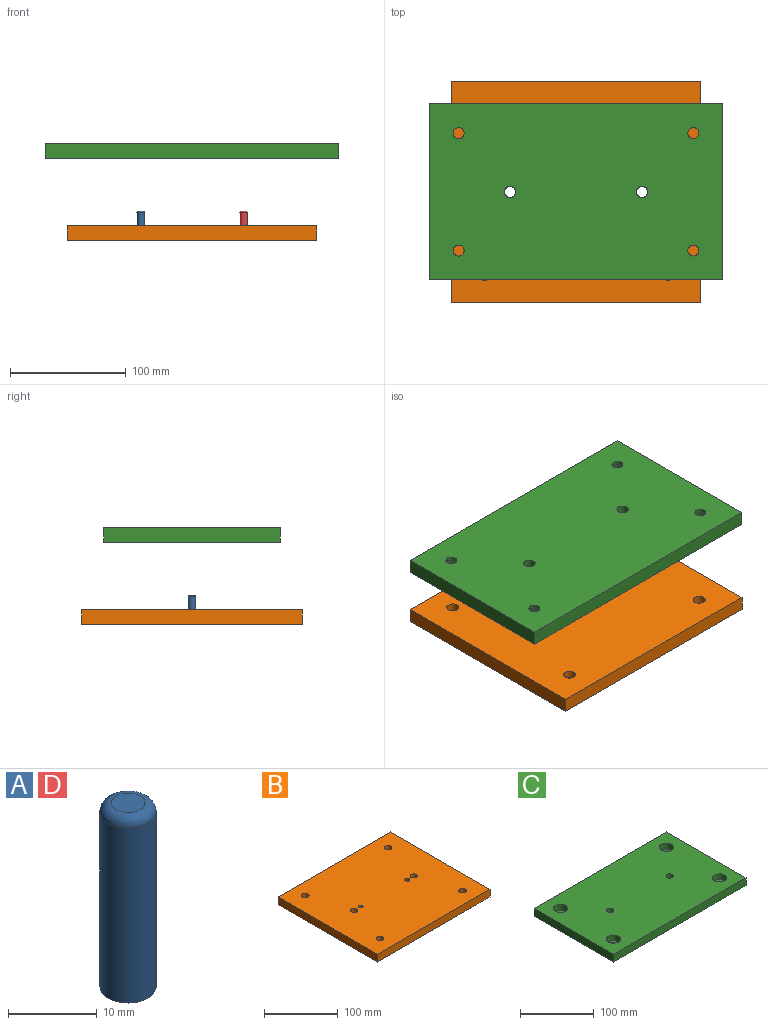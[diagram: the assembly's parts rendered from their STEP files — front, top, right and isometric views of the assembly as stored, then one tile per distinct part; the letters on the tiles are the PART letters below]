
ASSEMBLY  parts=4 mates=3
PART A: 4 faces, bbox 6.9x6.9x25.4 mm
  f0: cylinder r=3.17mm len=24.13mm, axis (0,0,-1), area 481.4mm2, adj f2,f3
  f1: plane 3.81x3.81mm, normal (0,0,1), area 11.4mm2, adj f3
  f2: plane 6.35x6.35mm, normal (0,0,-1), area 31.7mm2, adj f0
  f3: torus R=1.91mm, axis (0,0,1), area 34mm2, adj f0,f1
PART B: 22 faces, bbox 215.9x190.5x12.7 mm
  f0: plane 190.5x12.7mm, normal (-1,0,0), area 2419.3mm2, adj f1,f3,f4,f5
  f1: plane 215.9x12.7mm, normal (0,-1,0), area 2741.9mm2, adj f0,f2,f4,f5
  f2: plane 190.5x12.7mm, normal (1,0,0), area 2419.3mm2, adj f1,f3,f4,f5
  f3: plane 215.9x12.7mm, normal (0,1,0), area 2741.9mm2, adj f0,f2,f4,f5
  f4: plane 215.9x190.5mm, normal (0,0,1), area 40598.8mm2, adj f0,f1,f2,f3,f8,f11,f14,f17
  f5: plane 215.9x190.5mm, normal (0,0,-1), area 40791.3mm2, adj f0,f1,f2,f3,f6,f9,f12,f15
  f6: cylinder r=3.24mm len=6.48mm, axis (0,0,1), area 116.3mm2, adj f5,f7
  f7: plane 10.16x10.16mm, normal (0,0,1), area 48.1mm2, adj f6,f8
  f8: cylinder r=5.08mm len=10.16mm, axis (0,0,1), area 223mm2, adj f4,f7
  f9: cylinder r=3.24mm len=6.48mm, axis (0,0,1), area 116.3mm2, adj f5,f10
  f10: plane 10.16x10.16mm, normal (0,0,1), area 48.1mm2, adj f9,f11
  f11: cylinder r=5.08mm len=10.16mm, axis (0,0,1), area 223mm2, adj f4,f10
  f12: cylinder r=3.24mm len=6.48mm, axis (0,0,1), area 116.3mm2, adj f5,f13
  f13: plane 10.16x10.16mm, normal (0,0,1), area 48.1mm2, adj f12,f14
  f14: cylinder r=5.08mm len=10.16mm, axis (0,0,1), area 223mm2, adj f4,f13
  f15: cylinder r=3.24mm len=6.48mm, axis (0,0,1), area 116.3mm2, adj f5,f16
  f16: plane 10.16x10.16mm, normal (0,0,1), area 48.1mm2, adj f15,f17
  f17: cylinder r=5.08mm len=10.16mm, axis (0,0,1), area 223mm2, adj f4,f16
  f18: cylinder r=3.17mm len=12.7mm, axis (0,0,1), area 253.4mm2, adj f4,f5
  f19: cylinder r=3.17mm len=12.7mm, axis (0,0,1), area 253.4mm2, adj f4,f5
  f20: cylinder r=4.76mm len=12.7mm, axis (0,0,1), area 380mm2, adj f4,f5
  f21: cylinder r=4.76mm len=12.7mm, axis (0,0,1), area 380mm2, adj f4,f5
PART C: 20 faces, bbox 254x152.4x12.7 mm
  f0: plane 152.4x12.7mm, normal (-1,0,0), area 1935.5mm2, adj f1,f3,f4,f5
  f1: plane 254x12.7mm, normal (0,-1,0), area 3225.8mm2, adj f0,f2,f4,f5
  f2: plane 152.4x12.7mm, normal (1,0,0), area 1935.5mm2, adj f1,f3,f4,f5
  f3: plane 254x12.7mm, normal (0,1,0), area 3225.8mm2, adj f0,f2,f4,f5
  f4: plane 254x152.4mm, normal (0,0,1), area 37412.2mm2, adj f0,f1,f2,f3,f8,f11,f14,f17
  f5: plane 254x152.4mm, normal (0,0,-1), area 38267.3mm2, adj f0,f1,f2,f3,f6,f9,f12,f15
  f6: cylinder r=4.76mm len=9.53mm, axis (0,0,1), area 95mm2, adj f5,f7
  f7: plane 19.05x19.05mm, normal (0,0,1), area 213.8mm2, adj f6,f8
  f8: cylinder r=9.53mm len=19.05mm, axis (0,0,1), area 570mm2, adj f4,f7
  f9: cylinder r=4.76mm len=9.53mm, axis (0,0,1), area 95mm2, adj f5,f10
  f10: plane 19.05x19.05mm, normal (0,0,1), area 213.8mm2, adj f9,f11
  f11: cylinder r=9.53mm len=19.05mm, axis (0,0,1), area 570mm2, adj f4,f10
  f12: cylinder r=4.76mm len=9.53mm, axis (0,0,1), area 95mm2, adj f5,f13
  f13: plane 19.05x19.05mm, normal (0,0,1), area 213.8mm2, adj f12,f14
  f14: cylinder r=9.53mm len=19.05mm, axis (0,0,1), area 570mm2, adj f4,f13
  f15: cylinder r=4.76mm len=9.53mm, axis (0,0,1), area 95mm2, adj f5,f16
  f16: plane 19.05x19.05mm, normal (0,0,1), area 213.8mm2, adj f15,f17
  f17: cylinder r=9.53mm len=19.05mm, axis (0,0,1), area 570mm2, adj f4,f16
  f18: cylinder r=5mm len=12.7mm, axis (0,0,1), area 399.3mm2, adj f4,f5
  f19: cylinder r=5mm len=12.7mm, axis (0,0,1), area 399.3mm2, adj f4,f5
PART D: same geometry as A
PLACE A t=(63.5,95.25,0)mm
PLACE B at identity fixed
PLACE C rot(axis=(1,0,0),180deg) t=(-19.05,171.45,83.88)mm
PLACE D t=(152.4,95.25,0)mm
MATE planar A.f0 <-> B.f19  axis (0,0,-1) through (63.5,95.25,0)mm
MATE planar D.f0 <-> B.f18  axis (0,0,-1) through (152.4,95.25,0)mm
MATE slider C.f19 <-> B.f21  axis (0,0,-1) through (50.8,95.25,71.18)mm
